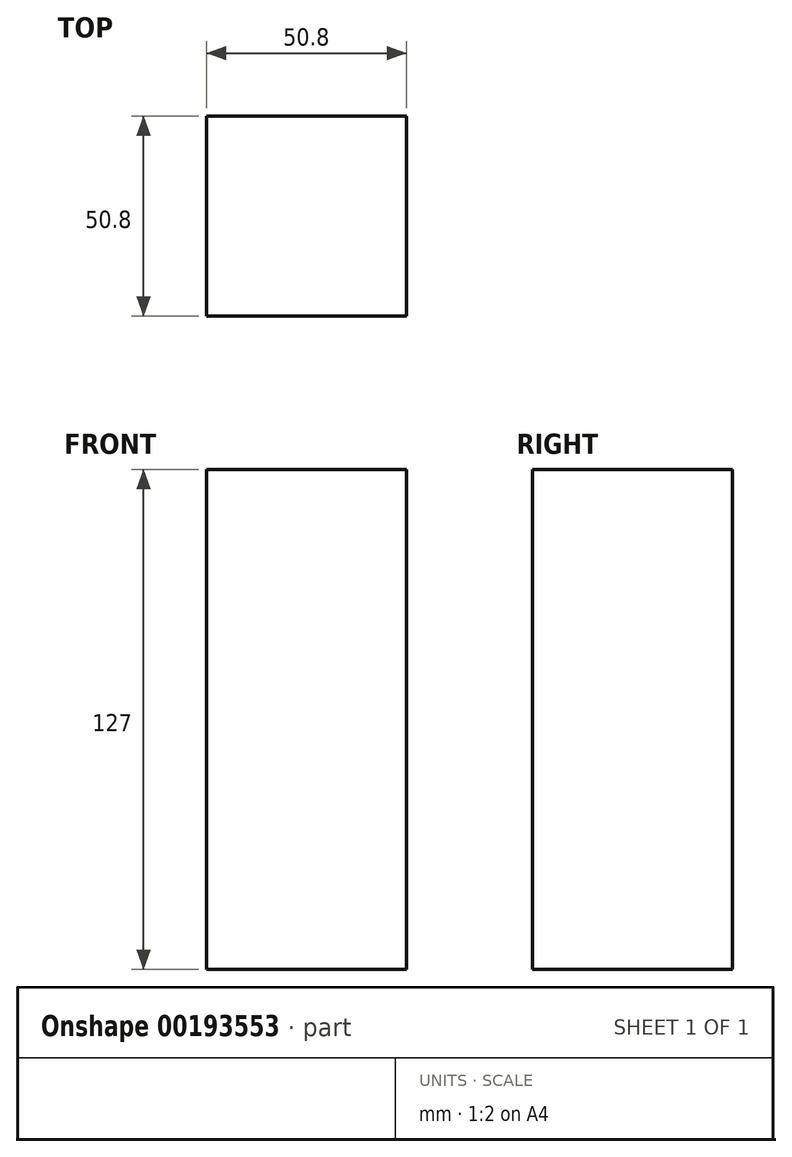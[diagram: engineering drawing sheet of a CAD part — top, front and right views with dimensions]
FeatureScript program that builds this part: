
annotation { "Feature Type Name" : "Feature", "Feature Type Description" : "" }
export const myFeature = defineFeature(function(context is Context, id is Id, definition is map)
    precondition{}
    {
        {
            var Q0;
            Q0=qCreatedBy(makeId("Top.planeOp"),FACE);
            var sketch = newSketch(context, id + "F0", { "sketchPlane" : qUnion([Q0])});
            skLineSegment(sketch, "E0.bottom", {"start": v(-25.4, 25.4) * mm, "end": v(25.4, 25.4) * mm});
            skLineSegment(sketch, "E0.top", {"start": v(-25.4, -25.4) * mm, "end": v(25.4, -25.4) * mm});
            skLineSegment(sketch, "E0.left", {"start": v(-25.4, 25.4) * mm, "end": v(-25.4, -25.4) * mm});
            skLineSegment(sketch, "E0.right", {"start": v(25.4, 25.4) * mm, "end": v(25.4, -25.4) * mm});
            skPoint(sketch, "E0.middle", {"position": v(0, 0) * mm});
            skSolve(sketch);
        }
        {
            var Q0;
            Q0=makeQuery(id+"F0.imprint","IMPRINT",FACE,{"disambiguationData":[TD([[makeQuery(id+"F0.imprint","IMPRINT",EDGE,{"derivedFrom":sQuery(id+"F0.wireOp",EDGE,"E0.bottom")}),-1.0]])]});
            extrude(context, id + "F1", {"entities" : qUnion([Q0]), "depth" : 127 * mm});
        }
    });
